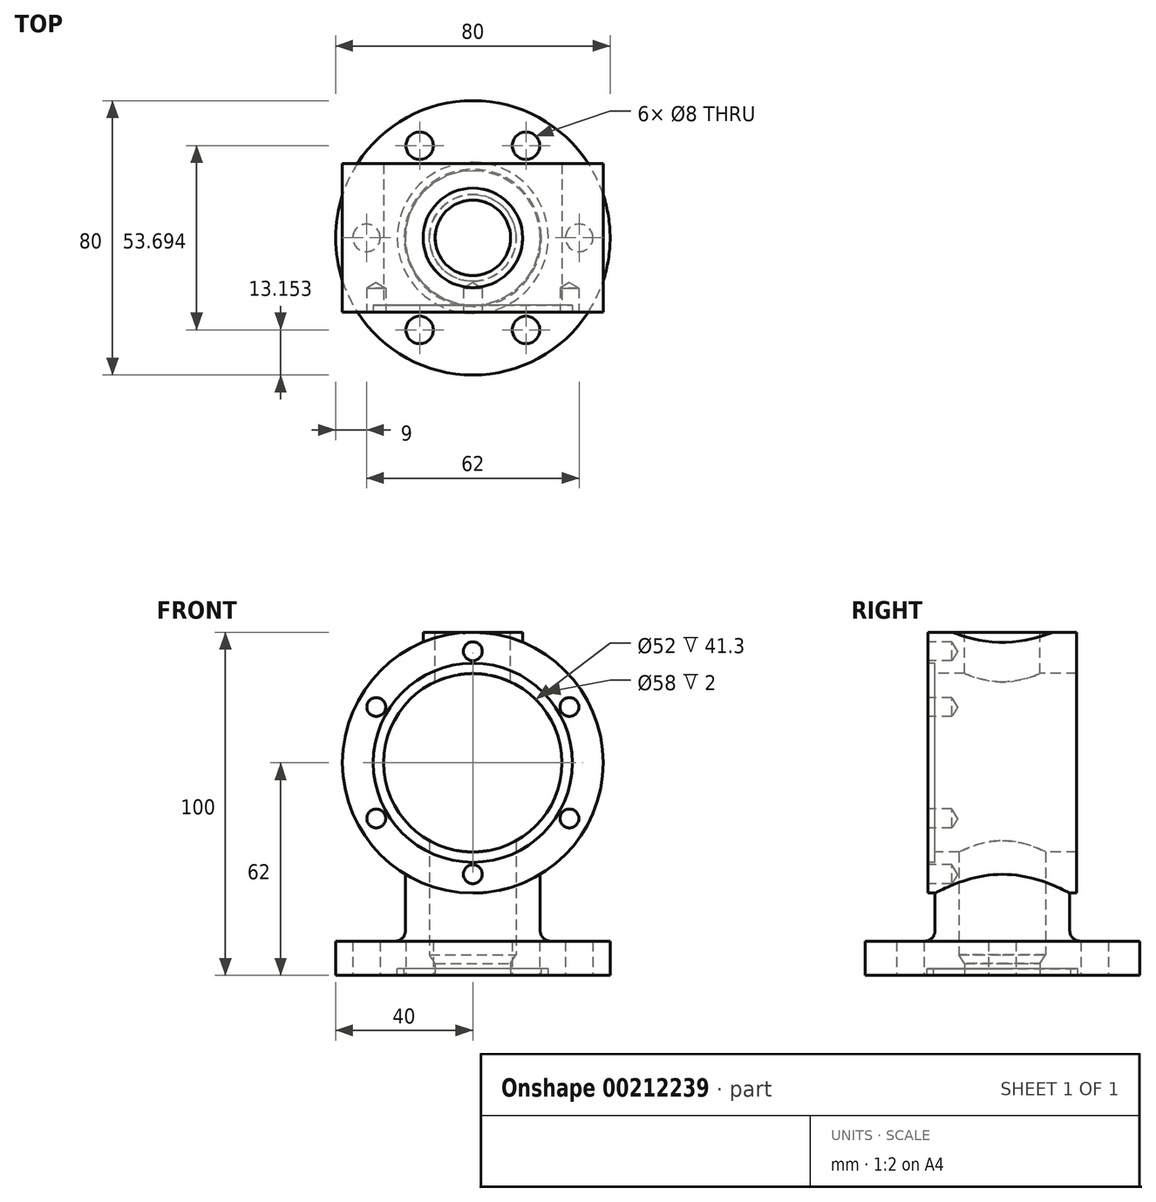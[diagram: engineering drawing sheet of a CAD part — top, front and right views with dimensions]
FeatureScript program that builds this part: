
annotation { "Feature Type Name" : "Feature", "Feature Type Description" : "" }
export const myFeature = defineFeature(function(context is Context, id is Id, definition is map)
    precondition{}
    {
        {
            var Q0;
            Q0=qCreatedBy(makeId("Front.planeOp"),FACE);
            var sketch = newSketch(context, id + "F0", { "sketchPlane" : qUnion([Q0])});
            skCircle(sketch, "E0", {"center": v(0, 0) * mm, "radius": 32.5 * mm, "construction": true});
            skCircle(sketch, "E1", {"center": v(0, 0) * mm, "radius": 38 * mm});
            skCircle(sketch, "E2", {"center": v(0, 0) * mm, "radius": 26 * mm});
            skCircle(sketch, "E3", {"center": v(0, 0) * mm, "radius": 29 * mm});
            skLineSegment(sketch, "E4", {"start": v(-19.65, -32.53) * mm, "end": v(-19.65, -49) * mm});
            skLineSegment(sketch, "E5", {"start": v(19.65, -32.53) * mm, "end": v(19.65, -49) * mm});
            skLineSegment(sketch, "E6.bottom", {"start": v(22.65, -52) * mm, "end": v(40, -52) * mm});
            skLineSegment(sketch, "E6.top", {"start": v(-40, -62) * mm, "end": v(40, -62) * mm});
            skLineSegment(sketch, "E6.left", {"start": v(-40, -52) * mm, "end": v(-40, -62) * mm});
            skLineSegment(sketch, "E6.right", {"start": v(40, -52) * mm, "end": v(40, -62) * mm});
            skLineSegment(sketch, "E7", {"start": v(0, 55.72) * mm, "end": v(0, -83.48) * mm});
            skPoint(sketch, "E8.newPointA", {"position": v(19.65, -52) * mm});
            skPoint(sketch, "E8.newPointB", {"position": v(-37.7, -52) * mm});
            skArc(sketch, "E8.filletArc", {"start": v(19.65, -49) * mm, "mid": v(20.53, -51.12) * mm, "end": v(22.65, -52) * mm});
            skLineSegment(sketch, "E9", {"start": v(-40, -52) * mm, "end": v(-22.65, -52) * mm});
            skPoint(sketch, "E10.newPointA", {"position": v(-19.65, -52) * mm});
            skPoint(sketch, "E10.newPointB", {"position": v(-19.65, -52) * mm});
            skArc(sketch, "E10.filletArc", {"start": v(-22.65, -52) * mm, "mid": v(-20.53, -51.12) * mm, "end": v(-19.65, -49) * mm});
            skLineSegment(sketch, "E11", {"start": v(-22, -62) * mm, "end": v(-22, -60) * mm});
            skLineSegment(sketch, "E12", {"start": v(-22, -60) * mm, "end": v(-20, -60) * mm});
            skLineSegment(sketch, "E13", {"start": v(-20, -60) * mm, "end": v(-20, -62) * mm});
            skSolve(sketch);
        }
        {
            var Q0;
            Q0=makeQuery(id+"F0.imprint","IMPRINT",FACE,{"disambiguationData":[TD([[makeQuery(id+"F0.imprint","IMPRINT",EDGE,{"derivedFrom":sQuery(id+"F0.wireOp",EDGE,"E3")}),-1.0]])]});
            var Q1;
            Q1=makeQuery(id+"F0.imprint","IMPRINT",FACE,{"disambiguationData":[TD([[makeQuery(id+"F0.imprint","IMPRINT",EDGE,{"derivedFrom":sQuery(id+"F0.wireOp",EDGE,"E2")}),-1.0]])]});
            extrude(context, id + "F1", {"entities" : qUnion([Q0, Q1]), "endBound" : BoundingType.SYMMETRIC, "oppositeDirection" : true, "depth" : 43.3 * mm});
        }
        {
            var Q0;
            Q0=qCreatedBy(makeId("Right.planeOp"),FACE);
            var sketch = newSketch(context, id + "F2", { "sketchPlane" : qUnion([Q0])});
            skLineSegment(sketch, "E14", {"start": v(0, 0) * mm, "end": v(0, 38) * mm});
            skLineSegment(sketch, "E15", {"start": v(0, 38) * mm, "end": v(-14.5, 38) * mm});
            skLineSegment(sketch, "E16", {"start": v(-14.5, 38) * mm, "end": v(-14.5, 28) * mm});
            skLineSegment(sketch, "E17", {"start": v(-14.5, 28) * mm, "end": v(0, 34) * mm});
            skSolve(sketch);
        }
        {
            var Q0;
            Q0 = qSketchRegion(id + "F2", true);
            var Q1;
            Q1=sQuery(id+"F2.wireOp",EDGE,"E14");
            revolve(context, id + "F3", {"operationType" : NewBodyOperationType.ADD, "entities" : qUnion([Q0]), "axis" : qUnion([Q1]), "revolveType" : RevolveType.FULL});
        }
        {
            var Q0;
            {var subQ4=sQuery(id+"F0.wireOp",EDGE,"E4");Q0=makeQuery(id+"F0.imprint","IMPRINT",FACE,{"disambiguationData":[TD([[makeQuery(id+"F0.imprint","IMPRINT",EDGE,{"derivedFrom":subQ4}),1.0]])]});}
            var Q1;
            Q1=sQuery(id+"F0.wireOp",EDGE,"E7");
            revolve(context, id + "F4", {"operationType" : NewBodyOperationType.ADD, "entities" : qUnion([Q0]), "axis" : qUnion([Q1]), "revolveType" : RevolveType.FULL});
        }
        {
            var Q0;
            {var subQ0=sQuery(id+"F0.wireOp",EDGE,"E11");Q0=makeQuery(id+"F0.imprint","IMPRINT",FACE,{"disambiguationData":[TD([[makeQuery(id+"F0.imprint","IMPRINT",EDGE,{"derivedFrom":subQ0}),-1.0]])]});}
            var Q1;
            Q1=sQuery(id+"F0.wireOp",EDGE,"E7");
            revolve(context, id + "F5", {"operationType" : NewBodyOperationType.REMOVE, "entities" : qUnion([Q0]), "axis" : qUnion([Q1]), "revolveType" : RevolveType.FULL, "oppositeDirection" : true});
        }
        {
            var Q0;
            Q0=makeQuery(id+"F1.opExtrude","CAP_FACE",FACE,{"disambiguationData":[OSD([sQuery(id+"F0.wireOp",EDGE,"E1"),sQuery(id+"F0.wireOp",EDGE,"E2")])],"isStart":true});
            var sketch = newSketch(context, id + "F6", { "sketchPlane" : qUnion([Q0])});
            skCircle(sketch, "E18", {"center": v(0, 0) * mm, "radius": 29 * mm});
            skSolve(sketch);
        }
        {
            var Q0;
            Q0 = qSketchRegion(id + "F6", true);
            extrude(context, id + "F7", {"entities" : qUnion([Q0]), "operationType" : NewBodyOperationType.REMOVE, "oppositeDirection" : true, "depth" : 2 * mm});
        }
        {
            var Q0;
            Q0=qCreatedBy(makeId("Right.planeOp"),FACE);
            var sketch = newSketch(context, id + "F8", { "sketchPlane" : qUnion([Q0])});
            skLineSegment(sketch, "E19", {"start": v(0, 49.3) * mm, "end": v(0, 22) * mm});
            skLineSegment(sketch, "E20", {"start": v(0, 2.21) * mm, "end": v(0, -68.9) * mm});
            skLineSegment(sketch, "E21", {"start": v(-11, -62) * mm, "end": v(-11, -58.5) * mm});
            skLineSegment(sketch, "E22", {"start": v(-11, -58.5) * mm, "end": v(-12.65, -56) * mm});
            skLineSegment(sketch, "E23", {"start": v(-12.65, -56) * mm, "end": v(-12.65, -20.08) * mm});
            skLineSegment(sketch, "E24", {"start": v(-12.65, -20.08) * mm, "end": v(0, -20.08) * mm});
            skLineSegment(sketch, "E25", {"start": v(-11, -62) * mm, "end": v(0, -62) * mm});
            skSolve(sketch);
        }
        {
            var Q0;
            Q0 = qSketchRegion(id + "F8", true);
            var Q1;
            Q1=sQuery(id+"F8.wireOp",EDGE,"E20");
            revolve(context, id + "F9", {"operationType" : NewBodyOperationType.REMOVE, "entities" : qUnion([Q0]), "axis" : qUnion([Q1]), "revolveType" : RevolveType.FULL, "oppositeDirection" : true});
        }
        {
            var Q0;
            Q0=makeQuery(id+"F6.imprint","IMPRINT",FACE,{"disambiguationData":[TD([[makeQuery(id+"F6.imprint","IMPRINT",EDGE,{"derivedFrom":sQuery(id+"F6.wireOp",EDGE,"E18")}),1.0]])]});
            var sketch = newSketch(context, id + "F10", { "sketchPlane" : qUnion([Q0])});
            skLineSegment(sketch, "E26", {"start": v(0, 0) * mm, "end": v(0, 32.5) * mm, "construction": true});
            skCircle(sketch, "E27.cCircle", {"center": v(0, 0) * mm, "radius": 32.5 * mm, "construction": true});
            skLineSegment(sketch, "E27.0", {"start": v(0, 32.5) * mm, "end": v(28.15, 16.25) * mm, "construction": true});
            skLineSegment(sketch, "E27.1", {"start": v(28.15, 16.25) * mm, "end": v(28.15, -16.25) * mm, "construction": true});
            skLineSegment(sketch, "E27.2", {"start": v(28.15, -16.25) * mm, "end": v(0, -32.5) * mm, "construction": true});
            skLineSegment(sketch, "E27.3", {"start": v(0, -32.5) * mm, "end": v(-28.15, -16.25) * mm, "construction": true});
            skLineSegment(sketch, "E27.4", {"start": v(-28.15, -16.25) * mm, "end": v(-28.15, 16.25) * mm, "construction": true});
            skLineSegment(sketch, "E27.5", {"start": v(-28.15, 16.25) * mm, "end": v(0, 32.5) * mm, "construction": true});
            skSolve(sketch);
        }
        {
            var Q0;
            Q0=sQuery(id+"F10.wireOp",VERTEX,"E27.0.start");
            var Q1;
            Q1=sQuery(id+"F10.wireOp",VERTEX,"E27.5.start");
            var Q2;
            Q2=sQuery(id+"F10.wireOp",VERTEX,"E27.3.end");
            var Q3;
            Q3=sQuery(id+"F10.wireOp",VERTEX,"E27.3.start");
            var Q4;
            Q4=sQuery(id+"F10.wireOp",VERTEX,"E27.2.start");
            var Q5;
            Q5=sQuery(id+"F10.wireOp",VERTEX,"E27.1.start");
            var Q6;
            Q6=makeQuery(id+"F1.opExtrude","SWEPT_BODY",BODY,{"disambiguationData":[OSD([sQuery(id+"F0.wireOp",EDGE,"E1"),sQuery(id+"F0.wireOp",EDGE,"E2")])]});
            hole(context, id + "F11", {"style" : HoleStyle.SIMPLE, "endStyle" : HoleEndStyle.BLIND, "standardTappedOrClearance" : lookupTablePath({ "standard" : "ISO", "fit" : "Normal", "size" : "M5", "type" : "Clearance" }), "standardBlindInLast" : lookupTablePath({ "fit" : "Standard", "standard" : "ISO", "size" : "M5", "type" : "Clearance" }), "holeDiameter" : 5.5 * mm, "holeDepth" : 7 * mm, "locations" : qUnion([Q0, Q1, Q2, Q3, Q4, Q5]), "scope" : qUnion([Q6])});
        }
        {
            var Q0;
            {var subQ0=sQuery(id+"F0.wireOp",EDGE,"E6.top");Q0=makeQuery(id+"F4.opRevolve","SWEPT_FACE",FACE,{"disambiguationData":[OSD([subQ0]),TDD([makeQuery(id+"F0.imprint","IMPRINT",EDGE,{"disambiguationData":[TD([[makeQuery(id+"F0.imprint","INTERSECT",VERTEX,{"derivedFrom":[subQ0,sQuery(id+"F0.wireOp",EDGE,"E6.left")]}),-1.0]])],"derivedFrom":subQ0})])]});}
            var sketch = newSketch(context, id + "F12", { "sketchPlane" : qUnion([Q0])});
            skLineSegment(sketch, "E28", {"start": v(0, 0) * mm, "end": v(0, 31) * mm, "construction": true});
            skCircle(sketch, "E29.cCircle", {"center": v(0, 0) * mm, "radius": 31 * mm, "construction": true});
            skLineSegment(sketch, "E29.0", {"start": v(15.5, 26.85) * mm, "end": v(31, 0) * mm});
            skLineSegment(sketch, "E29.1", {"start": v(31, 0) * mm, "end": v(15.5, -26.85) * mm});
            skLineSegment(sketch, "E29.2", {"start": v(15.5, -26.85) * mm, "end": v(-15.5, -26.85) * mm});
            skLineSegment(sketch, "E29.3", {"start": v(-15.5, -26.85) * mm, "end": v(-31, 0) * mm});
            skLineSegment(sketch, "E29.4", {"start": v(-31, 0) * mm, "end": v(-15.5, 26.85) * mm});
            skLineSegment(sketch, "E29.5", {"start": v(-15.5, 26.85) * mm, "end": v(15.5, 26.85) * mm});
            skSolve(sketch);
        }
        {
            var Q0;
            Q0=sQuery(id+"F12.wireOp",VERTEX,"E29.5.start");
            var Q1;
            Q1=sQuery(id+"F12.wireOp",VERTEX,"E29.0.start");
            var Q2;
            Q2=sQuery(id+"F12.wireOp",VERTEX,"E29.0.end");
            var Q3;
            Q3=sQuery(id+"F12.wireOp",VERTEX,"E29.1.end");
            var Q4;
            Q4=sQuery(id+"F12.wireOp",VERTEX,"E29.3.start");
            var Q5;
            Q5=sQuery(id+"F12.wireOp",VERTEX,"E29.4.start");
            var Q6;
            Q6=makeQuery(id+"F1.opExtrude","SWEPT_BODY",BODY,{"disambiguationData":[OSD([sQuery(id+"F0.wireOp",EDGE,"E1"),sQuery(id+"F0.wireOp",EDGE,"E2")])]});
            hole(context, id + "F13", {"style" : HoleStyle.SIMPLE, "endStyle" : HoleEndStyle.BLIND, "holeDiameter" : 8 * mm, "holeDepth" : 10 * mm, "locations" : qUnion([Q0, Q1, Q2, Q3, Q4, Q5]), "scope" : qUnion([Q6])});
        }
        {
            var Q0;
            Q0=makeQuery(id+"F3.opRevolve","SWEPT_FACE",FACE,{"disambiguationData":[OSD([sQuery(id+"F2.wireOp",EDGE,"E15")])]});
            var sketch = newSketch(context, id + "F14", { "sketchPlane" : qUnion([Q0])});
            skPoint(sketch, "E30", {"position": v(0, 0) * mm});
            skSolve(sketch);
        }
        {
            var Q0;
            Q0=sQuery(id+"F14.wireOp",VERTEX,"E30");
            var Q1;
            Q1=makeQuery(id+"F1.opExtrude","SWEPT_BODY",BODY,{"disambiguationData":[OSD([sQuery(id+"F0.wireOp",EDGE,"E1"),sQuery(id+"F0.wireOp",EDGE,"E2")])]});
            hole(context, id + "F15", {"style" : HoleStyle.SIMPLE, "endStyle" : HoleEndStyle.THROUGH, "standardTappedOrClearance" : lookupTablePath({ "standard" : "ISO", "fit" : "Normal", "size" : "M20", "type" : "Clearance" }), "standardBlindInLast" : lookupTablePath({ "fit" : "Standard", "standard" : "ISO", "size" : "M20", "type" : "Clearance" }), "holeDiameter" : 22 * mm, "locations" : qUnion([Q0]), "scope" : qUnion([Q1]), "isTappedThrough" : true});
        }
    });
